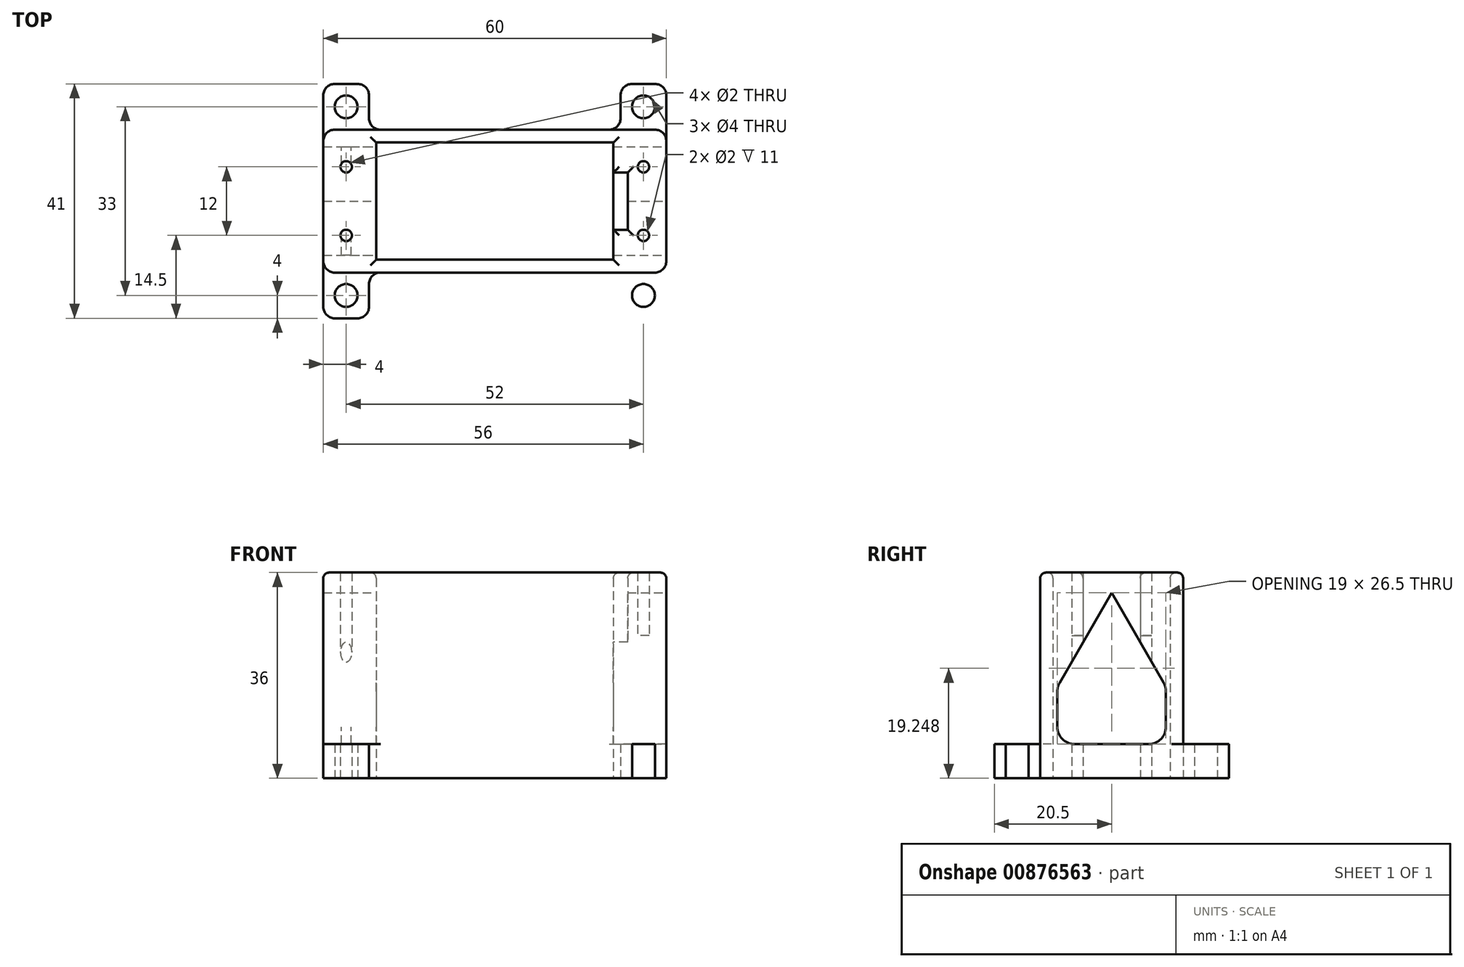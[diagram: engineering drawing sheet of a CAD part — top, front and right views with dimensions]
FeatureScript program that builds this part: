
annotation { "Feature Type Name" : "Feature", "Feature Type Description" : "" }
export const myFeature = defineFeature(function(context is Context, id is Id, definition is map)
    precondition{}
    {
        {
            var Q0;
            Q0=qCreatedBy(makeId("Top.planeOp"),FACE);
            var sketch = newSketch(context, id + "F0", { "sketchPlane" : qUnion([Q0])});
            skLineSegment(sketch, "E0.bottom", {"start": v(-20.75, -10.25) * mm, "end": v(20.75, -10.25) * mm});
            skLineSegment(sketch, "E0.top", {"start": v(-20.75, 10.25) * mm, "end": v(20.75, 10.25) * mm});
            skLineSegment(sketch, "E0.left", {"start": v(-20.75, -10.25) * mm, "end": v(-20.75, 10.25) * mm});
            skLineSegment(sketch, "E0.right", {"start": v(20.75, -10.25) * mm, "end": v(20.75, 10.25) * mm});
            skPoint(sketch, "E0.middle", {"position": v(0, 0) * mm});
            skLineSegment(sketch, "E1.bottom", {"start": v(20, -12.5) * mm, "end": v(-20, -12.5) * mm});
            skLineSegment(sketch, "E1.top", {"start": v(20, 12.5) * mm, "end": v(-20, 12.5) * mm});
            skLineSegment(sketch, "E1.left", {"start": v(30, -10.5) * mm, "end": v(30, 10.5) * mm});
            skLineSegment(sketch, "E1.right", {"start": v(-30, -10.5) * mm, "end": v(-30, 10.5) * mm});
            skLineSegment(sketch, "E2", {"start": v(0, 0) * mm, "end": v(26, 0) * mm, "construction": true});
            skPoint(sketch, "E2.endSnap0", {"position": v(20.75, 0) * mm});
            skLineSegment(sketch, "E3", {"start": v(26, 0) * mm, "end": v(26, 6) * mm, "construction": true});
            skLineSegment(sketch, "E4", {"start": v(26, 0) * mm, "end": v(26, -6) * mm, "construction": true});
            skCircle(sketch, "E5", {"center": v(26, 6) * mm, "radius": 1 * mm});
            skCircle(sketch, "E6", {"center": v(26, -6) * mm, "radius": 1 * mm});
            skCircle(sketch, "E7.MirrorC", {"center": v(-26, 6) * mm, "radius": 1 * mm});
            skCircle(sketch, "E8.MirrorC", {"center": v(-26, -6) * mm, "radius": 1 * mm});
            skLineSegment(sketch, "E9.bottom", {"start": v(-28, -12.5) * mm, "end": v(-22, -12.5) * mm});
            skLineSegment(sketch, "E9.top", {"start": v(-28, -20.5) * mm, "end": v(-24, -20.5) * mm});
            skLineSegment(sketch, "E9.left", {"start": v(-30, -12.5) * mm, "end": v(-30, -18.5) * mm});
            skLineSegment(sketch, "E9.right", {"start": v(-22, -14.5) * mm, "end": v(-22, -18.5) * mm});
            skLineSegment(sketch, "E10", {"start": v(-30, -12.5) * mm, "end": v(-22, -20.5) * mm, "construction": true});
            skCircle(sketch, "E11", {"center": v(-26, -16.5) * mm, "radius": 2 * mm});
            skLineSegment(sketch, "E12.MirrorCS", {"start": v(-28, 20.5) * mm, "end": v(-24, 20.5) * mm});
            skLineSegment(sketch, "E13.MirrorCS", {"start": v(-22, 14.5) * mm, "end": v(-22, 18.5) * mm});
            skCircle(sketch, "E14.MirrorC", {"center": v(-26, 16.5) * mm, "radius": 2 * mm});
            skLineSegment(sketch, "E15.MirrorCS", {"start": v(-30, 12.5) * mm, "end": v(-30, 18.5) * mm});
            skCircle(sketch, "E16.MirrorC", {"center": v(26, 16.5) * mm, "radius": 2 * mm});
            skCircle(sketch, "E17.MirrorC", {"center": v(26, -16.5) * mm, "radius": 2 * mm});
            skLineSegment(sketch, "E18.MirrorCS", {"start": v(22, -14.5) * mm, "end": v(22, -18.5) * mm});
            skLineSegment(sketch, "E19.MirrorCS", {"start": v(28, -20.5) * mm, "end": v(24, -20.5) * mm});
            skLineSegment(sketch, "E20.MirrorCS", {"start": v(30, -12.5) * mm, "end": v(30, -18.5) * mm});
            skLineSegment(sketch, "E21.MirrorCS", {"start": v(30, 12.5) * mm, "end": v(30, 18.5) * mm});
            skLineSegment(sketch, "E22.MirrorCS", {"start": v(28, 20.5) * mm, "end": v(24, 20.5) * mm});
            skLineSegment(sketch, "E23.MirrorCS", {"start": v(22, 14.5) * mm, "end": v(22, 18.5) * mm});
            skPoint(sketch, "E24.visualSharp", {"position": v(-22, -20.5) * mm});
            skArc(sketch, "E24.filletArc", {"start": v(-24, -20.5) * mm, "mid": v(-22.59, -19.91) * mm, "end": v(-22, -18.5) * mm});
            skPoint(sketch, "E25.visualSharp", {"position": v(-30, -20.5) * mm});
            skArc(sketch, "E25.filletArc", {"start": v(-30, -18.5) * mm, "mid": v(-29.41, -19.91) * mm, "end": v(-28, -20.5) * mm});
            skPoint(sketch, "E26.newPointA", {"position": v(-22, -12.5) * mm});
            skPoint(sketch, "E26.newPointB", {"position": v(-30, -12.5) * mm});
            skArc(sketch, "E26.filletArc", {"start": v(-20, -12.5) * mm, "mid": v(-21.41, -13.09) * mm, "end": v(-22, -14.5) * mm});
            skPoint(sketch, "E27.newPointA", {"position": v(22, -12.5) * mm});
            skPoint(sketch, "E27.newPointB", {"position": v(30, -12.5) * mm});
            skArc(sketch, "E27.filletArc", {"start": v(22, -14.5) * mm, "mid": v(21.41, -13.09) * mm, "end": v(20, -12.5) * mm});
            skPoint(sketch, "E28.visualSharp", {"position": v(22, -20.5) * mm});
            skArc(sketch, "E28.filletArc", {"start": v(22, -18.5) * mm, "mid": v(22.59, -19.91) * mm, "end": v(24, -20.5) * mm});
            skPoint(sketch, "E29.visualSharp", {"position": v(30, -20.5) * mm});
            skArc(sketch, "E29.filletArc", {"start": v(28, -20.5) * mm, "mid": v(29.41, -19.91) * mm, "end": v(30, -18.5) * mm});
            skPoint(sketch, "E30.visualSharp", {"position": v(30, 20.5) * mm});
            skArc(sketch, "E30.filletArc", {"start": v(30, 18.5) * mm, "mid": v(29.41, 19.91) * mm, "end": v(28, 20.5) * mm});
            skPoint(sketch, "E31.visualSharp", {"position": v(22, 20.5) * mm});
            skArc(sketch, "E31.filletArc", {"start": v(24, 20.5) * mm, "mid": v(22.59, 19.91) * mm, "end": v(22, 18.5) * mm});
            skPoint(sketch, "E32.newPointA", {"position": v(22, 12.5) * mm});
            skPoint(sketch, "E32.newPointB", {"position": v(30, 12.5) * mm});
            skArc(sketch, "E32.filletArc", {"start": v(20, 12.5) * mm, "mid": v(21.41, 13.09) * mm, "end": v(22, 14.5) * mm});
            skPoint(sketch, "E33.newPointA", {"position": v(-22, 12.5) * mm});
            skPoint(sketch, "E33.newPointB", {"position": v(-30, 12.5) * mm});
            skArc(sketch, "E33.filletArc", {"start": v(-22, 14.5) * mm, "mid": v(-21.41, 13.09) * mm, "end": v(-20, 12.5) * mm});
            skPoint(sketch, "E34.visualSharp", {"position": v(-22, 20.5) * mm});
            skArc(sketch, "E34.filletArc", {"start": v(-22, 18.5) * mm, "mid": v(-22.59, 19.91) * mm, "end": v(-24, 20.5) * mm});
            skPoint(sketch, "E35.visualSharp", {"position": v(-30, 20.5) * mm});
            skArc(sketch, "E35.filletArc", {"start": v(-28, 20.5) * mm, "mid": v(-29.41, 19.91) * mm, "end": v(-30, 18.5) * mm});
            skLineSegment(sketch, "E36", {"start": v(-22, -12.5) * mm, "end": v(-20, -12.5) * mm});
            skLineSegment(sketch, "E37", {"start": v(20, 12.5) * mm, "end": v(22, 12.5) * mm});
            skLineSegment(sketch, "E38", {"start": v(22, 12.5) * mm, "end": v(28, 12.5) * mm});
            skLineSegment(sketch, "E39", {"start": v(20, -12.5) * mm, "end": v(22, -12.5) * mm});
            skLineSegment(sketch, "E40", {"start": v(22, -12.5) * mm, "end": v(28, -12.5) * mm});
            skArc(sketch, "E41.filletArc", {"start": v(-30, -10.5) * mm, "mid": v(-29.41, -11.91) * mm, "end": v(-28, -12.5) * mm});
            skLineSegment(sketch, "E42", {"start": v(-30, -10.5) * mm, "end": v(-30, -12.5) * mm});
            skArc(sketch, "E43.filletArc", {"start": v(30, 10.5) * mm, "mid": v(29.41, 11.91) * mm, "end": v(28, 12.5) * mm});
            skArc(sketch, "E44.filletArc", {"start": v(28, -12.5) * mm, "mid": v(29.41, -11.91) * mm, "end": v(30, -10.5) * mm});
            skLineSegment(sketch, "E45", {"start": v(30, 10.5) * mm, "end": v(30, 12.5) * mm});
            skLineSegment(sketch, "E46", {"start": v(30, -12.5) * mm, "end": v(30, -10.5) * mm});
            skLineSegment(sketch, "E47", {"start": v(-20, 12.5) * mm, "end": v(-28, 12.5) * mm});
            skArc(sketch, "E48.filletArc", {"start": v(-28, 12.5) * mm, "mid": v(-29.41, 11.91) * mm, "end": v(-30, 10.5) * mm});
            skLineSegment(sketch, "E49", {"start": v(-30, 12.5) * mm, "end": v(-30, 10.5) * mm});
            skLineSegment(sketch, "E50", {"start": v(20.75, 0) * mm, "end": v(20.75, 5) * mm});
            skLineSegment(sketch, "E51", {"start": v(20.75, 5) * mm, "end": v(23.25, 5) * mm});
            skLineSegment(sketch, "E52", {"start": v(20.75, 0) * mm, "end": v(20.75, -5) * mm});
            skLineSegment(sketch, "E53.bottom", {"start": v(20.75, -5) * mm, "end": v(23.25, -5) * mm});
            skLineSegment(sketch, "E53.left", {"start": v(20.75, -5) * mm, "end": v(20.75, 5) * mm});
            skLineSegment(sketch, "E53.right", {"start": v(23.25, -5) * mm, "end": v(23.25, 5) * mm});
            skSolve(sketch);
        }
        {
            var Q0;
            Q0=makeQuery(id+"F0.imprint","IMPRINT",FACE,{"disambiguationData":[TD([[makeQuery(id+"F0.imprint","IMPRINT",EDGE,{"derivedFrom":sQuery(id+"F0.wireOp",EDGE,"E0.bottom")}),-1.0]])]});
            extrude(context, id + "F1", {"entities" : qUnion([Q0]), "depth" : 36 * mm, "offsetDistance" : 25 * mm});
        }
        {
            var Q0;
            Q0=makeQuery(id+"F0.imprint","IMPRINT",FACE,{"disambiguationData":[TD([[makeQuery(id+"F0.imprint","IMPRINT",EDGE,{"derivedFrom":sQuery(id+"F0.wireOp",EDGE,"E9.bottom")}),-1.0]])]});
            var Q1;
            Q1=makeQuery(id+"F0.imprint","IMPRINT",FACE,{"disambiguationData":[TD([[makeQuery(id+"F0.imprint","IMPRINT",EDGE,{"derivedFrom":sQuery(id+"F0.wireOp",EDGE,"E17.MirrorC")}),1.0]])]});
            var Q2;
            Q2=makeQuery(id+"F0.imprint","IMPRINT",FACE,{"disambiguationData":[TD([[makeQuery(id+"F0.imprint","IMPRINT",EDGE,{"derivedFrom":sQuery(id+"F0.wireOp",EDGE,"E16.MirrorC")}),-1.0]])]});
            var Q3;
            Q3=makeQuery(id+"F0.imprint","IMPRINT",FACE,{"disambiguationData":[TD([[makeQuery(id+"F0.imprint","IMPRINT",EDGE,{"derivedFrom":sQuery(id+"F0.wireOp",EDGE,"E12.MirrorCS")}),-1.0]])]});
            var Q4;
            Q4=makeQuery(id+"F0.imprint","IMPRINT",FACE,{"disambiguationData":[TD([[makeQuery(id+"F0.imprint","IMPRINT",EDGE,{"derivedFrom":sQuery(id+"F0.wireOp",EDGE,"E53.bottom")}),1.0]])]});
            extrude(context, id + "F2", {"entities" : qUnion([Q0, Q1, Q2, Q3, Q4]), "operationType" : NewBodyOperationType.ADD, "depth" : 6 * mm, "offsetDistance" : 25 * mm});
        }
        {
            var Q0;
            Q0=makeQuery(id+"F1.opExtrude","CAP_EDGE",EDGE,{"disambiguationData":[OSD([sQuery(id+"F0.wireOp",EDGE,"E0.top")])],"isStart":false});
            var Q1;
            Q1=makeQuery(id+"F1.opExtrude","CAP_EDGE",EDGE,{"disambiguationData":[OSD([sQuery(id+"F0.wireOp",EDGE,"E0.left")])],"isStart":false});
            var Q2;
            Q2=makeQuery(id+"F1.opExtrude","CAP_EDGE",EDGE,{"disambiguationData":[OSD([sQuery(id+"F0.wireOp",EDGE,"E0.right")])],"isStart":false});
            var Q3;
            Q3=makeQuery(id+"F1.opExtrude","CAP_EDGE",EDGE,{"disambiguationData":[OSD([sQuery(id+"F0.wireOp",EDGE,"E0.bottom")])],"isStart":false});
            var Q4;
            Q4=makeQuery(id+"F1.opExtrude","CAP_EDGE",EDGE,{"disambiguationData":[OSD([sQuery(id+"F0.wireOp",EDGE,"E53.bottom")])],"isStart":false});
            var Q5;
            Q5=makeQuery(id+"F1.opExtrude","CAP_EDGE",EDGE,{"disambiguationData":[OSD([sQuery(id+"F0.wireOp",EDGE,"E53.right")])],"isStart":false});
            var Q6;
            Q6=makeQuery(id+"F1.opExtrude","CAP_EDGE",EDGE,{"disambiguationData":[OSD([sQuery(id+"F0.wireOp",EDGE,"E51")])],"isStart":false});
            fillet(context, id + "F3", {"entities" : qUnion([Q0, Q1, Q2, Q3, Q4, Q5, Q6]), "radius" : 1 * mm, "tangentPropagation" : true, "allowEdgeOverflow" : false});
        }
        {
            var Q0;
            Q0=makeQuery(id+"F1.opExtrude","CAP_EDGE",EDGE,{"disambiguationData":[OSD([sQuery(id+"F0.wireOp",EDGE,"E1.left")])],"isStart":false});
            var Q1;
            Q1=makeQuery(id+"F1.opExtrude","CAP_EDGE",EDGE,{"disambiguationData":[OSD([sQuery(id+"F0.wireOp",EDGE,"E1.top"),sQuery(id+"F0.wireOp",EDGE,"E37"),sQuery(id+"F0.wireOp",EDGE,"E38"),sQuery(id+"F0.wireOp",EDGE,"E47")])],"isStart":false});
            var Q2;
            Q2=makeQuery(id+"F1.opExtrude","CAP_EDGE",EDGE,{"disambiguationData":[OSD([sQuery(id+"F0.wireOp",EDGE,"E1.bottom"),sQuery(id+"F0.wireOp",EDGE,"E9.bottom"),sQuery(id+"F0.wireOp",EDGE,"E36"),sQuery(id+"F0.wireOp",EDGE,"E39"),sQuery(id+"F0.wireOp",EDGE,"E40")])],"isStart":false});
            var Q3;
            Q3=makeQuery(id+"F1.opExtrude","CAP_EDGE",EDGE,{"disambiguationData":[OSD([sQuery(id+"F0.wireOp",EDGE,"E44.filletArc")])],"isStart":false});
            var Q4;
            Q4=makeQuery(id+"F1.opExtrude","CAP_EDGE",EDGE,{"disambiguationData":[OSD([sQuery(id+"F0.wireOp",EDGE,"E43.filletArc")])],"isStart":false});
            var Q5;
            Q5=makeQuery(id+"F1.opExtrude","CAP_EDGE",EDGE,{"disambiguationData":[OSD([sQuery(id+"F0.wireOp",EDGE,"E1.right")])],"isStart":false});
            var Q6;
            Q6=makeQuery(id+"F1.opExtrude","CAP_EDGE",EDGE,{"disambiguationData":[OSD([sQuery(id+"F0.wireOp",EDGE,"E48.filletArc")])],"isStart":false});
            var Q7;
            Q7=makeQuery(id+"F1.opExtrude","CAP_EDGE",EDGE,{"disambiguationData":[OSD([sQuery(id+"F0.wireOp",EDGE,"E41.filletArc")])],"isStart":false});
            fillet(context, id + "F4", {"entities" : qUnion([Q0, Q1, Q2, Q3, Q4, Q5, Q6, Q7]), "radius" : 1 * mm, "tangentPropagation" : true, "allowEdgeOverflow" : false});
        }
        {
            var Q0;
            Q0=makeQuery(id+"F0.imprint","IMPRINT",FACE,{"disambiguationData":[TD([[makeQuery(id+"F0.imprint","IMPRINT",EDGE,{"derivedFrom":sQuery(id+"F0.wireOp",EDGE,"E7.MirrorC")}),-1.0]])]});
            var Q1;
            Q1=makeQuery(id+"F0.imprint","IMPRINT",FACE,{"disambiguationData":[TD([[makeQuery(id+"F0.imprint","IMPRINT",EDGE,{"derivedFrom":sQuery(id+"F0.wireOp",EDGE,"E8.MirrorC")}),-1.0]])]});
            var Q2;
            Q2=makeQuery(id+"F0.imprint","IMPRINT",FACE,{"disambiguationData":[TD([[makeQuery(id+"F0.imprint","IMPRINT",EDGE,{"derivedFrom":sQuery(id+"F0.wireOp",EDGE,"E6")}),1.0]])]});
            var Q3;
            Q3=makeQuery(id+"F0.imprint","IMPRINT",FACE,{"disambiguationData":[TD([[makeQuery(id+"F0.imprint","IMPRINT",EDGE,{"derivedFrom":sQuery(id+"F0.wireOp",EDGE,"E5")}),1.0]])]});
            var Q4;
            Q4=sQuery(id+"F0.wireOp",EDGE,"E6");
            var Q5;
            Q5=sQuery(id+"F0.wireOp",EDGE,"E5");
            var Q6;
            Q6=sQuery(id+"F0.wireOp",EDGE,"E7.MirrorC");
            var Q7;
            Q7=sQuery(id+"F0.wireOp",EDGE,"E8.MirrorC");
            extrude(context, id + "F5", {"entities" : qUnion([Q0, Q1, Q2, Q3]), "operationType" : NewBodyOperationType.ADD, "surfaceOperationType" : NewSurfaceOperationType.ADD, "surfaceEntities" : qUnion([Q4, Q5, Q6, Q7]), "depth" : 25 * mm, "offsetDistance" : 25 * mm});
        }
        {
            var Q0;
            Q0=makeQuery(id+"F2.boolean.opBoolean","MERGE",FACE,{"derivedFrom":[makeQuery(id+"F1.opExtrude","SWEPT_FACE",FACE,{"disambiguationData":[OSD([sQuery(id+"F0.wireOp",EDGE,"E1.left")])]}),makeQuery(id+"F2.opExtrude","SWEPT_FACE",FACE,{"disambiguationData":[OSD([sQuery(id+"F0.wireOp",EDGE,"E20.MirrorCS")])]}),makeQuery(id+"F2.opExtrude","SWEPT_FACE",FACE,{"disambiguationData":[OSD([sQuery(id+"F0.wireOp",EDGE,"E21.MirrorCS")])]})]});
            var sketch = newSketch(context, id + "F6", { "sketchPlane" : qUnion([Q0])});
            skLineSegment(sketch, "E54", {"start": v(9.5, 6) * mm, "end": v(-9.5, 6) * mm});
            skLineSegment(sketch, "E55", {"start": v(-9.5, 6) * mm, "end": v(-9.5, 16) * mm});
            skLineSegment(sketch, "E56", {"start": v(-9.5, 16) * mm, "end": v(0, 32.5) * mm});
            skLineSegment(sketch, "E57", {"start": v(0, 32.5) * mm, "end": v(9.5, 16) * mm});
            skLineSegment(sketch, "E58", {"start": v(9.5, 16) * mm, "end": v(9.5, 6) * mm});
            skSolve(sketch);
        }
        {
            var Q0;
            Q0=makeQuery(id+"F6.imprint","IMPRINT",FACE,{"disambiguationData":[TD([[makeQuery(id+"F6.imprint","IMPRINT",EDGE,{"derivedFrom":sQuery(id+"F6.wireOp",EDGE,"E54")}),-1.0]])]});
            extrude(context, id + "F7", {"entities" : qUnion([Q0]), "operationType" : NewBodyOperationType.REMOVE, "oppositeDirection" : true, "depth" : 100 * mm, "offsetDistance" : 25 * mm});
        }
        {
            var Q0;
            {var subQ0=sQuery(id+"F6.wireOp",EDGE,"E54");var subQ1=sQuery(id+"F6.wireOp",EDGE,"E55");Q0=makeQuery(id+"F7.boolean.opBoolean","COPY",EDGE,{"disambiguationData":[TD([makeQuery(id+"F1.opExtrude","SWEPT_FACE",FACE,{"disambiguationData":[OSD([sQuery(id+"F0.wireOp",EDGE,"E0.right")])]})])],"derivedFrom":makeQuery(id+"F7.opExtrude","SWEPT_EDGE",EDGE,{"disambiguationData":[OSD([subQ0,subQ1])]})});}
            var Q1;
            {var subQ0=sQuery(id+"F6.wireOp",EDGE,"E54");var subQ1=sQuery(id+"F6.wireOp",EDGE,"E58");Q1=makeQuery(id+"F7.boolean.opBoolean","COPY",EDGE,{"disambiguationData":[TD([makeQuery(id+"F1.opExtrude","SWEPT_FACE",FACE,{"disambiguationData":[OSD([sQuery(id+"F0.wireOp",EDGE,"E0.right")])]})])],"derivedFrom":makeQuery(id+"F7.opExtrude","SWEPT_EDGE",EDGE,{"disambiguationData":[OSD([subQ0,subQ1])]})});}
            var Q2;
            {var subQ0=sQuery(id+"F6.wireOp",EDGE,"E58");var subQ1=sQuery(id+"F6.wireOp",EDGE,"E54");Q2=makeQuery(id+"F7.boolean.opBoolean","COPY",EDGE,{"disambiguationData":[TD([makeQuery(id+"F1.opExtrude","SWEPT_FACE",FACE,{"disambiguationData":[OSD([sQuery(id+"F0.wireOp",EDGE,"E0.left")])]})])],"derivedFrom":makeQuery(id+"F7.opExtrude","SWEPT_EDGE",EDGE,{"disambiguationData":[OSD([subQ1,subQ0])]})});}
            var Q3;
            {var subQ0=sQuery(id+"F6.wireOp",EDGE,"E54");var subQ1=sQuery(id+"F6.wireOp",EDGE,"E55");Q3=makeQuery(id+"F7.boolean.opBoolean","COPY",EDGE,{"disambiguationData":[TD([makeQuery(id+"F1.opExtrude","SWEPT_FACE",FACE,{"disambiguationData":[OSD([sQuery(id+"F0.wireOp",EDGE,"E0.left")])]})])],"derivedFrom":makeQuery(id+"F7.opExtrude","SWEPT_EDGE",EDGE,{"disambiguationData":[OSD([subQ0,subQ1])]})});}
            var Q4;
            {var subQ0=sQuery(id+"F6.wireOp",EDGE,"E57");var subQ1=sQuery(id+"F6.wireOp",EDGE,"E58");Q4=makeQuery(id+"F7.boolean.opBoolean","COPY",EDGE,{"disambiguationData":[TD([makeQuery(id+"F1.opExtrude","SWEPT_FACE",FACE,{"disambiguationData":[OSD([sQuery(id+"F0.wireOp",EDGE,"E0.right")])]})])],"derivedFrom":makeQuery(id+"F7.opExtrude","SWEPT_EDGE",EDGE,{"disambiguationData":[OSD([subQ0,subQ1])]})});}
            var Q5;
            {var subQ0=sQuery(id+"F6.wireOp",EDGE,"E57");var subQ1=sQuery(id+"F6.wireOp",EDGE,"E58");Q5=makeQuery(id+"F7.boolean.opBoolean","COPY",EDGE,{"disambiguationData":[TD([makeQuery(id+"F1.opExtrude","SWEPT_FACE",FACE,{"disambiguationData":[OSD([sQuery(id+"F0.wireOp",EDGE,"E0.left")])]})])],"derivedFrom":makeQuery(id+"F7.opExtrude","SWEPT_EDGE",EDGE,{"disambiguationData":[OSD([subQ0,subQ1])]})});}
            var Q6;
            {var subQ0=sQuery(id+"F6.wireOp",EDGE,"E55");var subQ1=sQuery(id+"F6.wireOp",EDGE,"E56");Q6=makeQuery(id+"F7.boolean.opBoolean","COPY",EDGE,{"disambiguationData":[TD([makeQuery(id+"F1.opExtrude","SWEPT_FACE",FACE,{"disambiguationData":[OSD([sQuery(id+"F0.wireOp",EDGE,"E0.right")])]})])],"derivedFrom":makeQuery(id+"F7.opExtrude","SWEPT_EDGE",EDGE,{"disambiguationData":[OSD([subQ0,subQ1])]})});}
            var Q7;
            {var subQ0=sQuery(id+"F6.wireOp",EDGE,"E55");var subQ1=sQuery(id+"F6.wireOp",EDGE,"E56");Q7=makeQuery(id+"F7.boolean.opBoolean","COPY",EDGE,{"disambiguationData":[TD([makeQuery(id+"F1.opExtrude","SWEPT_FACE",FACE,{"disambiguationData":[OSD([sQuery(id+"F0.wireOp",EDGE,"E0.left")])]})])],"derivedFrom":makeQuery(id+"F7.opExtrude","SWEPT_EDGE",EDGE,{"disambiguationData":[OSD([subQ0,subQ1])]})});}
            fillet(context, id + "F8", {"entities" : qUnion([Q0, Q1, Q2, Q3, Q4, Q5, Q6, Q7]), "radius" : 3 * mm, "tangentPropagation" : true, "allowEdgeOverflow" : false});
        }
    });
